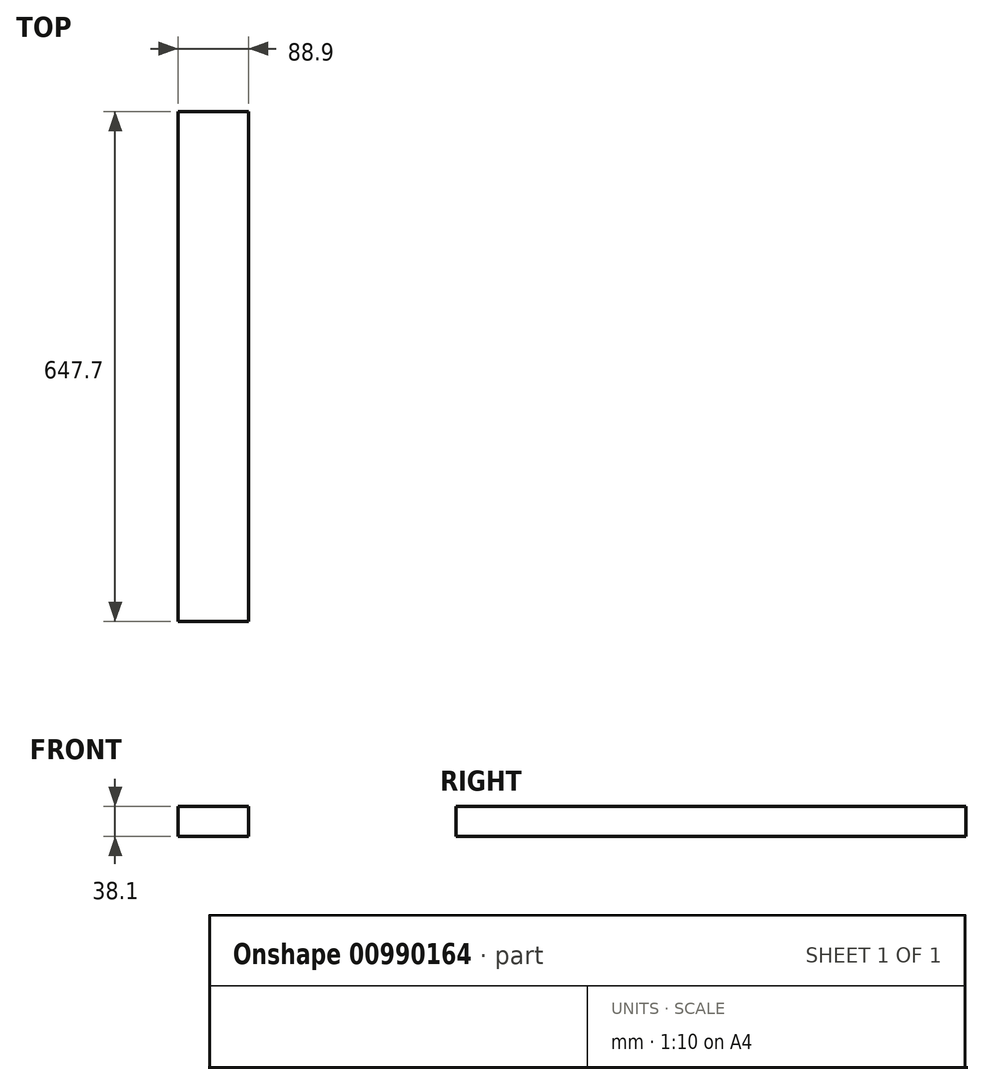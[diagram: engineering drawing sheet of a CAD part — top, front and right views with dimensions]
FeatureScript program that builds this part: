
annotation { "Feature Type Name" : "Feature", "Feature Type Description" : "" }
export const myFeature = defineFeature(function(context is Context, id is Id, definition is map)
    precondition{}
    {
        {
            assignVariable(context, id + "F0", {"name" : "w", "anyValue" : 38.1 * mm});
        }
        {
            var Q0;
            Q0=qCreatedBy(makeId("Top.planeOp"),FACE);
            var sketch = newSketch(context, id + "F1", { "sketchPlane" : qUnion([Q0])});
            skLineSegment(sketch, "E0.bottom", {"start": v(44.45, 323.85) * mm, "end": v(-44.45, 323.85) * mm});
            skLineSegment(sketch, "E0.top", {"start": v(44.45, -323.85) * mm, "end": v(-44.45, -323.85) * mm});
            skLineSegment(sketch, "E0.left", {"start": v(44.45, 323.85) * mm, "end": v(44.45, -323.85) * mm});
            skLineSegment(sketch, "E0.right", {"start": v(-44.45, 323.85) * mm, "end": v(-44.45, -323.85) * mm});
            skPoint(sketch, "E0.middle", {"position": v(0, 0) * mm});
            skSolve(sketch);
        }
        {
            var Q0;
            Q0=qSketchRegion(id+"F1",true);
            extrude(context, id + "F2", {"entities" : qUnion([Q0]), "depth" : getVariable(context, 'w'), "offsetDistance" : 25.4 * mm});
        }
    });
